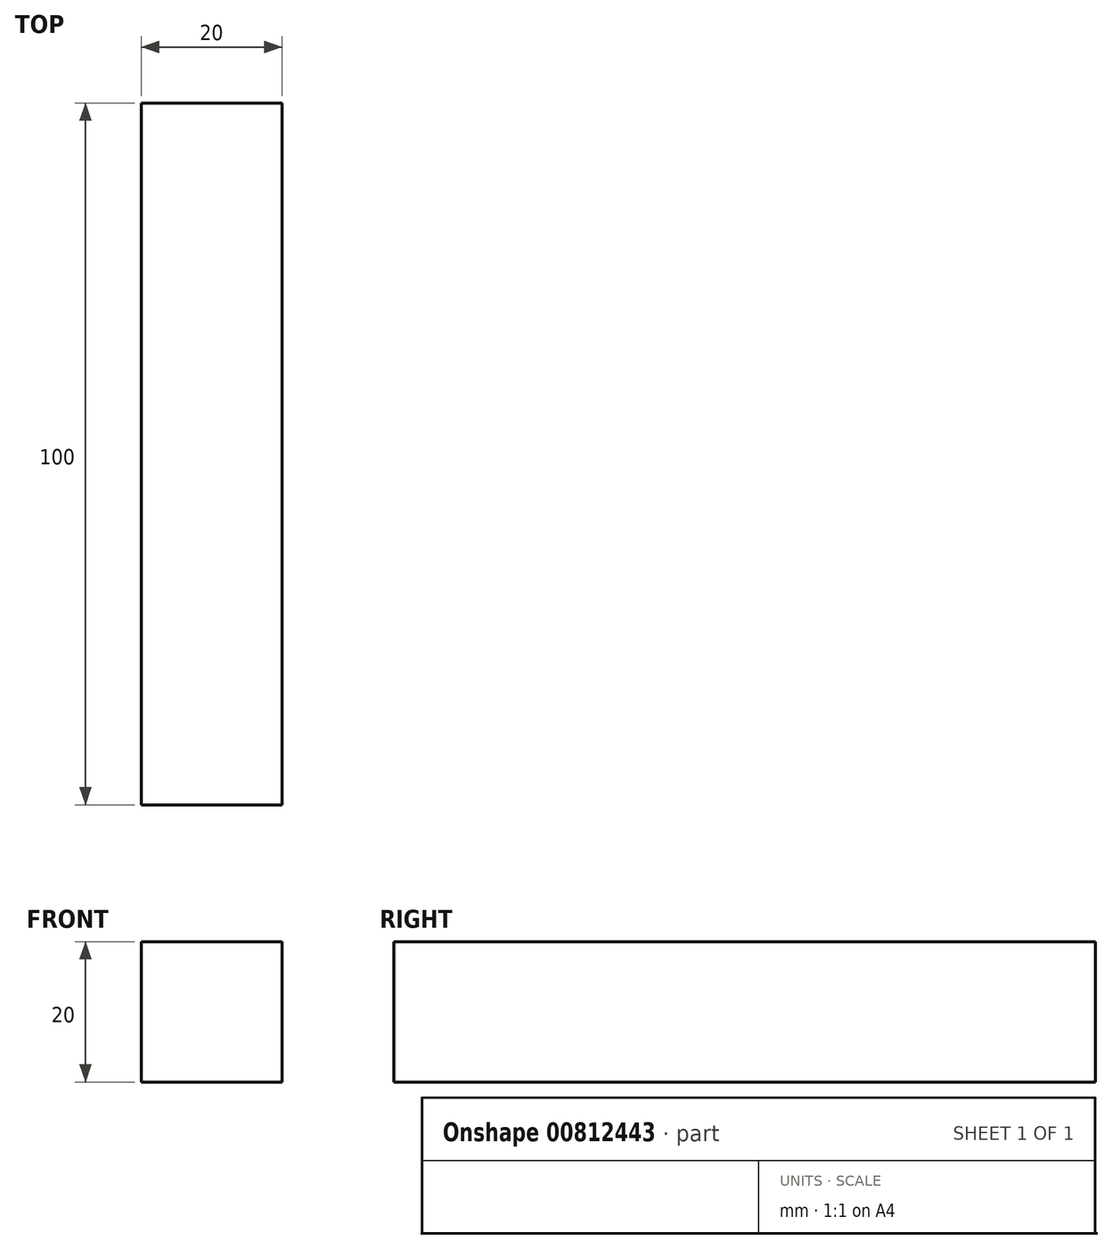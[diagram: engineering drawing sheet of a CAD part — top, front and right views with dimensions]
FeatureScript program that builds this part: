
annotation { "Feature Type Name" : "Feature", "Feature Type Description" : "" }
export const myFeature = defineFeature(function(context is Context, id is Id, definition is map)
    precondition{}
    {
        {
            var Q0;
            Q0=qCreatedBy(makeId("Front.planeOp"),FACE);
            var sketch = newSketch(context, id + "F0", { "sketchPlane" : qUnion([Q0])});
            skLineSegment(sketch, "E0.bottom", {"start": v(-10, 10) * mm, "end": v(10, 10) * mm});
            skLineSegment(sketch, "E0.top", {"start": v(-10, -10) * mm, "end": v(10, -10) * mm});
            skLineSegment(sketch, "E0.left", {"start": v(-10, 10) * mm, "end": v(-10, -10) * mm});
            skLineSegment(sketch, "E0.right", {"start": v(10, 10) * mm, "end": v(10, -10) * mm});
            skSolve(sketch);
        }
        {
            var Q0;
            Q0 = qSketchRegion(id + "F0", true);
            extrude(context, id + "F1", {"entities" : qUnion([Q0]), "depth" : 100 * mm, "offsetDistance" : 25 * mm});
        }
    });
